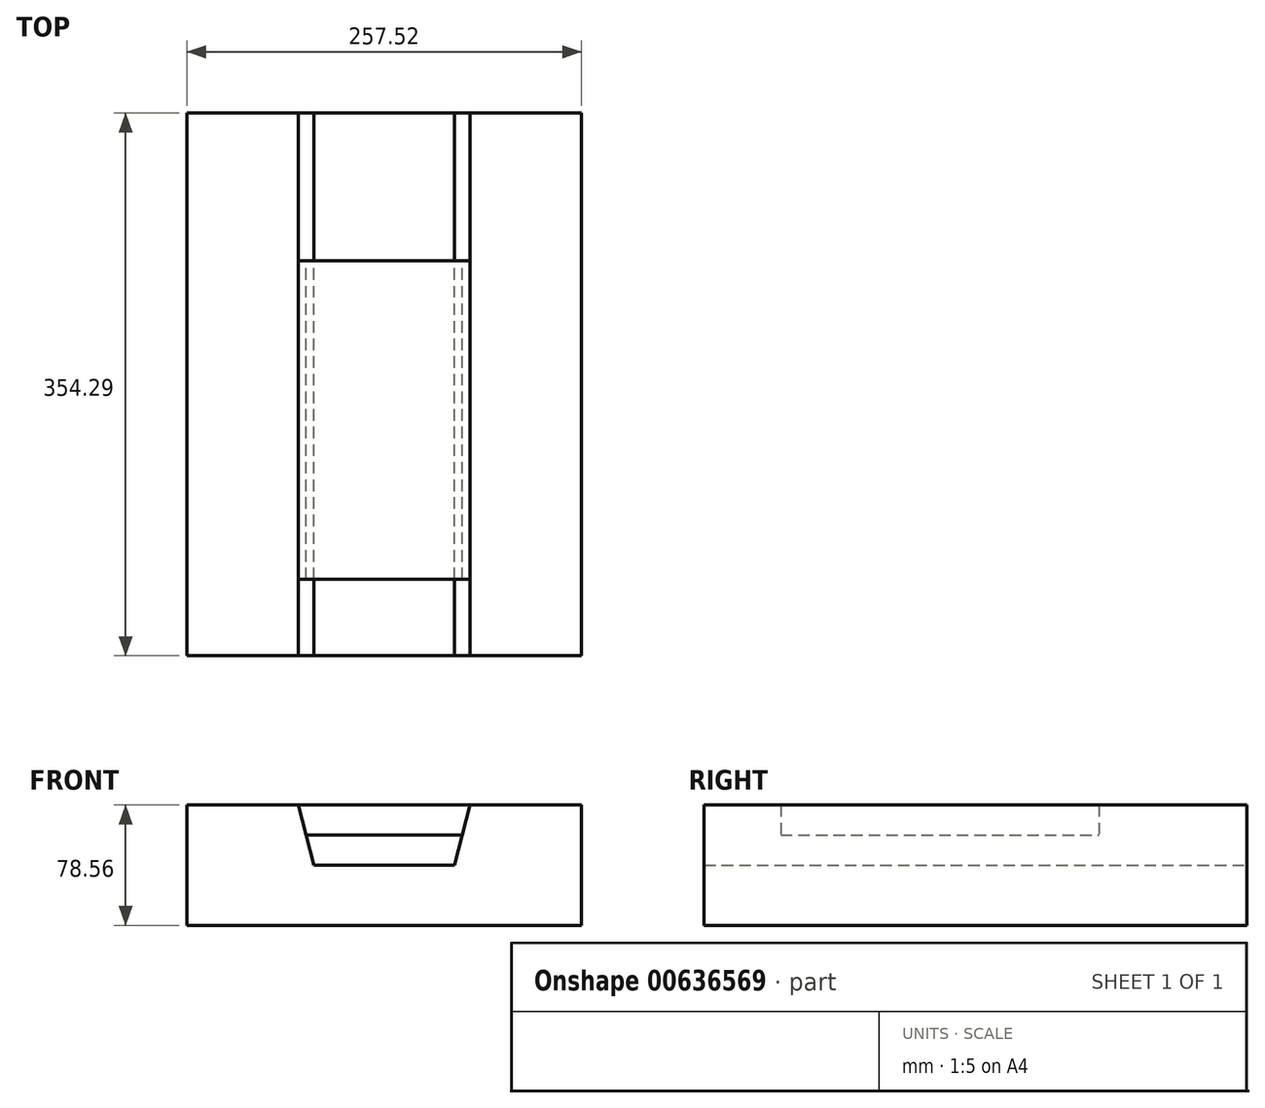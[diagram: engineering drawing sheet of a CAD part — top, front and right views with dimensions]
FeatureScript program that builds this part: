
annotation { "Feature Type Name" : "Feature", "Feature Type Description" : "" }
export const myFeature = defineFeature(function(context is Context, id is Id, definition is map)
    precondition{}
    {
        {
            var Q0;
            Q0=qCreatedBy(makeId("Front.planeOp"),FACE);
            var sketch = newSketch(context, id + "F0", { "sketchPlane" : qUnion([Q0])});
            skLineSegment(sketch, "E0.bottom", {"start": v(128.76, 39.28) * mm, "end": v(34.92, 39.28) * mm});
            skLineSegment(sketch, "E0.top", {"start": v(128.76, -39.28) * mm, "end": v(-128.76, -39.28) * mm});
            skLineSegment(sketch, "E0.left", {"start": v(128.76, 39.28) * mm, "end": v(128.76, -39.28) * mm});
            skLineSegment(sketch, "E0.right", {"start": v(-128.76, 39.28) * mm, "end": v(-128.76, -39.28) * mm});
            skPoint(sketch, "E1.top.end.orphan", {"position": v(-34.92, -114.21) * mm});
            skPoint(sketch, "E1.top.start.orphan", {"position": v(34.92, -114.21) * mm});
            skLineSegment(sketch, "E2.trimOffspring", {"start": v(-34.92, 39.28) * mm, "end": v(-128.76, 39.28) * mm});
            skPoint(sketch, "E1.bottom.end.orphan", {"position": v(-34.92, 114.21) * mm});
            skPoint(sketch, "E1.bottom.start.orphan", {"position": v(34.92, 114.21) * mm});
            skLineSegment(sketch, "E3", {"start": v(34.92, 39.28) * mm, "end": v(-34.92, 39.28) * mm});
            skSolve(sketch);
        }
        {
            var Q0;
            Q0 = qSketchRegion(id + "F0", true);
            extrude(context, id + "F1", {"entities" : qUnion([Q0]), "depth" : 354.3 * mm, "offsetDistance" : 25 * mm});
        }
        {
            var Q0;
            Q0=makeQuery(id+"F1.opExtrude","CAP_FACE",FACE,{"disambiguationData":[OSD([sQuery(id+"F0.wireOp",EDGE,"E0.bottom"),sQuery(id+"F0.wireOp",EDGE,"E0.top"),sQuery(id+"F0.wireOp",EDGE,"E0.left"),sQuery(id+"F0.wireOp",EDGE,"E0.right"),sQuery(id+"F0.wireOp",EDGE,"E2.trimOffspring"),sQuery(id+"F0.wireOp",EDGE,"E3")])],"isStart":true});
            var sketch = newSketch(context, id + "F2", { "sketchPlane" : qUnion([Q0])});
            skLineSegment(sketch, "E4.bottom", {"start": v(0, 0) * mm, "end": v(45.83, 0) * mm});
            skLineSegment(sketch, "E4.top", {"start": v(0, 120.07) * mm, "end": v(45.83, 120.07) * mm});
            skLineSegment(sketch, "E4.right", {"start": v(45.83, 106.3) * mm, "end": v(45.83, 120.07) * mm});
            skLineSegment(sketch, "E5.MirrorCS", {"start": v(0, 120.07) * mm, "end": v(-45.83, 120.07) * mm});
            skLineSegment(sketch, "E6.MirrorCS", {"start": v(-45.83, 106.3) * mm, "end": v(-45.83, 120.07) * mm});
            skLineSegment(sketch, "E7.MirrorCS", {"start": v(0, 0) * mm, "end": v(-45.83, 0) * mm});
            skLineSegment(sketch, "E8", {"start": v(-45.83, 0) * mm, "end": v(-71.63, 98.54) * mm});
            skLineSegment(sketch, "E9", {"start": v(-71.63, 98.54) * mm, "end": v(-45.83, 106.3) * mm});
            skLineSegment(sketch, "E10.MirrorCS", {"start": v(45.83, 0) * mm, "end": v(71.63, 98.54) * mm});
            skLineSegment(sketch, "E11.MirrorCS", {"start": v(71.63, 98.54) * mm, "end": v(45.83, 106.3) * mm});
            skPoint(sketch, "E12.orphan", {"position": v(0, 120.07) * mm});
            skSolve(sketch);
        }
        {
            var Q0;
            Q0 = qSketchRegion(id + "F2", true);
            extrude(context, id + "F3", {"entities" : qUnion([Q0]), "operationType" : NewBodyOperationType.REMOVE, "oppositeDirection" : true, "depth" : 507.26 * mm, "offsetDistance" : 25 * mm});
        }
        {
            var Q0;
            Q0=qCreatedBy(makeId("Front.planeOp"),FACE);
            cPlane(context, id + "F4", {"entities" : qUnion([Q0]), "cplaneType" : CPlaneType.OFFSET, "offset" : 200.39 * mm, "width" : 150 * mm, "height" : 150 * mm});
        }
        {
            var Q0;
            Q0=qCreatedBy(id+"F4.planeOp",FACE);
            var sketch = newSketch(context, id + "F5", { "sketchPlane" : qUnion([Q0])});
            skLineSegment(sketch, "E13.0", {"start": v(56.12, 39.28) * mm, "end": v(50.98, 19.64) * mm});
            skLineSegment(sketch, "E14.0", {"start": v(-56.12, 39.28) * mm, "end": v(-50.98, 19.64) * mm});
            skLineSegment(sketch, "E15", {"start": v(-56.12, 39.28) * mm, "end": v(56.12, 39.28) * mm});
            skLineSegment(sketch, "E16", {"start": v(-50.98, 19.64) * mm, "end": v(50.98, 19.64) * mm});
            skPoint(sketch, "E17.start.orphan", {"position": v(-45.83, 0) * mm});
            skPoint(sketch, "E18.orphan", {"position": v(45.83, 0) * mm});
            skSolve(sketch);
        }
        {
            var Q0;
            Q0 = qSketchRegion(id + "F5", true);
            extrude(context, id + "F6", {"entities" : qUnion([Q0]), "endBound" : BoundingType.SYMMETRIC, "depth" : 207.82 * mm, "offsetDistance" : 25 * mm});
        }
    });
